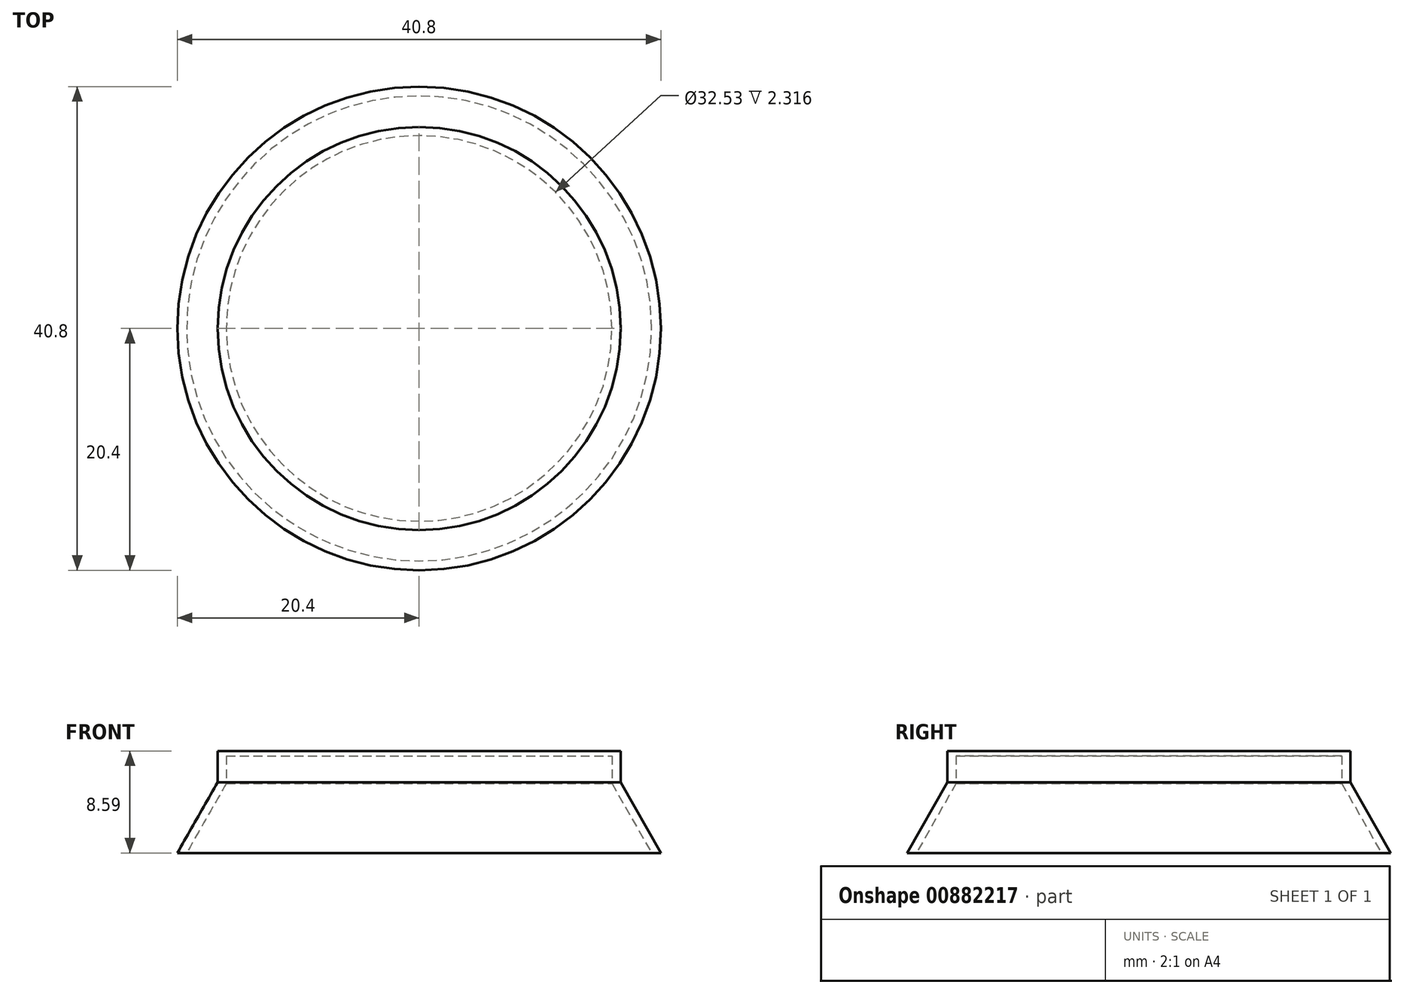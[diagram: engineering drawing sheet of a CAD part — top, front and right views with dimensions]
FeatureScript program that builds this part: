
annotation { "Feature Type Name" : "Feature", "Feature Type Description" : "" }
export const myFeature = defineFeature(function(context is Context, id is Id, definition is map)
    precondition{}
    {
        {
            var Q0;
            Q0=qCreatedBy(makeId("Right.planeOp"),FACE);
            var sketch = newSketch(context, id + "F0", { "sketchPlane" : qUnion([Q0])});
            skLineSegment(sketch, "E0", {"start": v(0, 0) * mm, "end": v(-17, 0) * mm});
            skLineSegment(sketch, "E1", {"start": v(-17, 0) * mm, "end": v(-17, -2.63) * mm});
            skLineSegment(sketch, "E2", {"start": v(-17, -2.63) * mm, "end": v(-20.4, -8.6) * mm});
            skLineSegment(sketch, "E3", {"start": v(-20.4, -8.6) * mm, "end": v(-19.62, -8.6) * mm});
            skLineSegment(sketch, "E4", {"start": v(-19.62, -8.6) * mm, "end": v(-16.26, -2.72) * mm});
            skLineSegment(sketch, "E5", {"start": v(-16.26, -2.72) * mm, "end": v(-16.26, -0.4) * mm});
            skLineSegment(sketch, "E6", {"start": v(-16.26, -0.4) * mm, "end": v(0, -0.4) * mm});
            skLineSegment(sketch, "E7", {"start": v(0, -0.4) * mm, "end": v(0, 0) * mm});
            skSolve(sketch);
        }
        {
            var Q0;
            Q0 = qSketchRegion(id + "F0", true);
            var Q1;
            Q1=sQuery(id+"F0.wireOp",EDGE,"E7");
            revolve(context, id + "F1", {"surfaceOperationType" : NewSurfaceOperationType.NEW, "entities" : qUnion([Q0]), "axis" : qUnion([Q1]), "revolveType" : RevolveType.FULL});
        }
        {
            var Q0;
            Q0=qCreatedBy(makeId("Right.planeOp"),FACE);
            var sketch = newSketch(context, id + "F2", { "sketchPlane" : qUnion([Q0])});
            skLineSegment(sketch, "E8", {"start": v(56.63, 6.95) * mm, "end": v(39.63, 6.95) * mm});
            skLineSegment(sketch, "E9", {"start": v(39.63, 6.95) * mm, "end": v(39.63, 4.32) * mm});
            skLineSegment(sketch, "E10", {"start": v(39.63, 4.32) * mm, "end": v(36.23, -1.64) * mm});
            skLineSegment(sketch, "E11", {"start": v(36.23, -1.64) * mm, "end": v(37.01, -1.64) * mm});
            skLineSegment(sketch, "E12", {"start": v(37.01, -1.64) * mm, "end": v(40.36, 4.24) * mm});
            skLineSegment(sketch, "E13", {"start": v(40.36, 4.24) * mm, "end": v(40.36, 6.55) * mm});
            skLineSegment(sketch, "E14", {"start": v(40.36, 6.55) * mm, "end": v(56.63, 6.55) * mm});
            skLineSegment(sketch, "E15", {"start": v(56.63, 6.95) * mm, "end": v(56.63, 6.55) * mm});
            skSolve(sketch);
        }
    });
